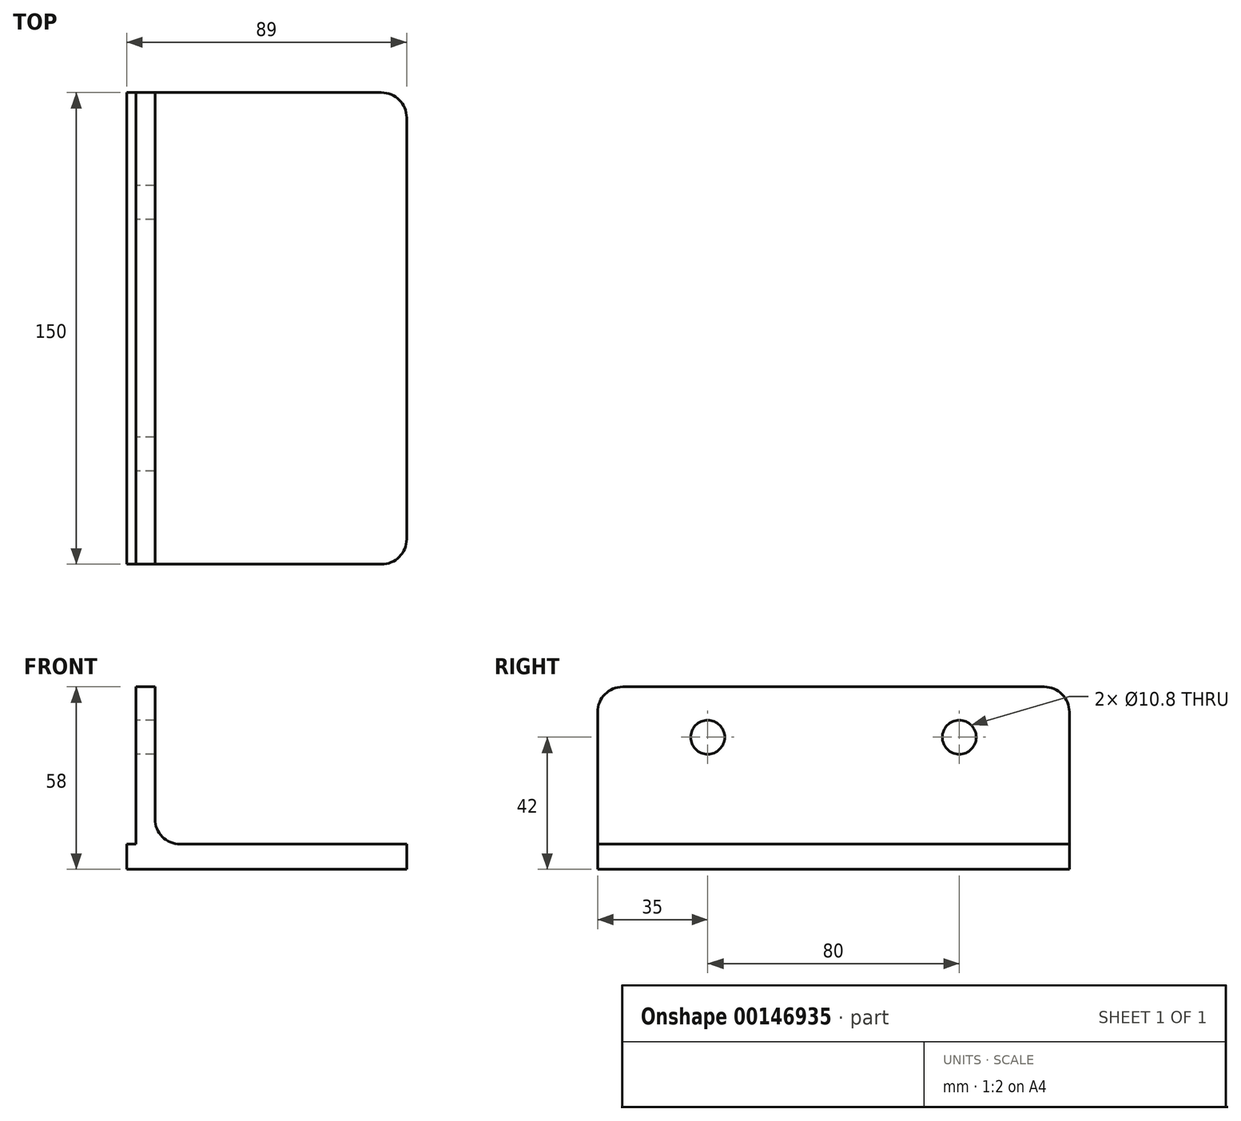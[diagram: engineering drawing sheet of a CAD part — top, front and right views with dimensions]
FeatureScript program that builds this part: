
annotation { "Feature Type Name" : "Feature", "Feature Type Description" : "" }
export const myFeature = defineFeature(function(context is Context, id is Id, definition is map)
    precondition{}
    {
        {
            var Q0;
            Q0=qCreatedBy(makeId("Front.planeOp"),FACE);
            var sketch = newSketch(context, id + "F0", { "sketchPlane" : qUnion([Q0])});
            skLineSegment(sketch, "E0", {"start": v(-3, 0) * mm, "end": v(0, 0) * mm});
            skLineSegment(sketch, "E1", {"start": v(0, 50) * mm, "end": v(6, 50) * mm});
            skLineSegment(sketch, "E2", {"start": v(6, 50) * mm, "end": v(6, 0) * mm});
            skLineSegment(sketch, "E3", {"start": v(6, 0) * mm, "end": v(86, 0) * mm});
            skLineSegment(sketch, "E4", {"start": v(86, 0) * mm, "end": v(86, -8) * mm});
            skLineSegment(sketch, "E5", {"start": v(-3, -8) * mm, "end": v(-3, 0) * mm});
            skLineSegment(sketch, "E6", {"start": v(-3, -8) * mm, "end": v(86, -8) * mm});
            skLineSegment(sketch, "E7", {"start": v(0, 50) * mm, "end": v(0, 0) * mm});
            skSolve(sketch);
        }
        {
            var Q0;
            Q0=makeQuery(id+"F0.imprint","IMPRINT",FACE,{"disambiguationData":[TD([[makeQuery(id+"F0.imprint","IMPRINT",EDGE,{"derivedFrom":sQuery(id+"F0.wireOp",EDGE,"E0")}),-1.0]])]});
            extrude(context, id + "F1", {"entities" : qUnion([Q0]), "endBound" : BoundingType.SYMMETRIC, "oppositeDirection" : true, "depth" : 150 * mm});
        }
        {
            var Q0;
            Q0=makeQuery(id+"F1.opExtrude","CAP_EDGE",EDGE,{"disambiguationData":[OSD([sQuery(id+"F0.wireOp",EDGE,"E4")])],"isStart":true});
            var Q1;
            Q1=makeQuery(id+"F1.opExtrude","CAP_EDGE",EDGE,{"disambiguationData":[OSD([sQuery(id+"F0.wireOp",EDGE,"E4")])],"isStart":false});
            var Q2;
            Q2=makeQuery(id+"F1.opExtrude","CAP_EDGE",EDGE,{"disambiguationData":[OSD([sQuery(id+"F0.wireOp",EDGE,"E1")])],"isStart":true});
            var Q3;
            Q3=makeQuery(id+"F1.opExtrude","CAP_EDGE",EDGE,{"disambiguationData":[OSD([sQuery(id+"F0.wireOp",EDGE,"E1")])],"isStart":false});
            var Q4;
            Q4=makeQuery(id+"F1.opExtrude","SWEPT_EDGE",EDGE,{"disambiguationData":[OSD([sQuery(id+"F0.wireOp",EDGE,"E2"),sQuery(id+"F0.wireOp",EDGE,"E3")])]});
            fillet(context, id + "F2", {"entities" : qUnion([Q0, Q1, Q2, Q3, Q4]), "radius" : 8 * mm, "tangentPropagation" : true, "allowEdgeOverflow" : false});
        }
        {
            var Q0;
            Q0=qCreatedBy(makeId("Right.planeOp"),FACE);
            var sketch = newSketch(context, id + "F3", { "sketchPlane" : qUnion([Q0])});
            skLineSegment(sketch, "E8", {"start": v(0, 0) * mm, "end": v(0, 34) * mm});
            skLineSegment(sketch, "E9", {"start": v(0, 34) * mm, "end": v(40, 34) * mm});
            skLineSegment(sketch, "E10", {"start": v(0, 34) * mm, "end": v(-40, 34) * mm});
            skCircle(sketch, "E11", {"center": v(-40, 34) * mm, "radius": 5.4 * mm});
            skCircle(sketch, "E12", {"center": v(40, 34) * mm, "radius": 5.4 * mm});
            skSolve(sketch);
        }
        {
            var Q0;
            Q0=makeQuery(id+"F3.imprint","IMPRINT",FACE,{"disambiguationData":[TD([[makeQuery(id+"F3.imprint","IMPRINT",EDGE,{"derivedFrom":sQuery(id+"F3.wireOp",EDGE,"E11")}),1.0]])]});
            var Q1;
            Q1=makeQuery(id+"F3.imprint","IMPRINT",FACE,{"disambiguationData":[TD([[makeQuery(id+"F3.imprint","IMPRINT",EDGE,{"derivedFrom":sQuery(id+"F3.wireOp",EDGE,"E12")}),1.0]])]});
            var Q2;
            Q2=sQuery(id+"F3.wireOp",EDGE,"E11");
            extrude(context, id + "F4", {"entities" : qUnion([Q0, Q1]), "operationType" : NewBodyOperationType.REMOVE, "surfaceEntities" : qUnion([Q2]), "depth" : 25 * mm});
        }
    });
